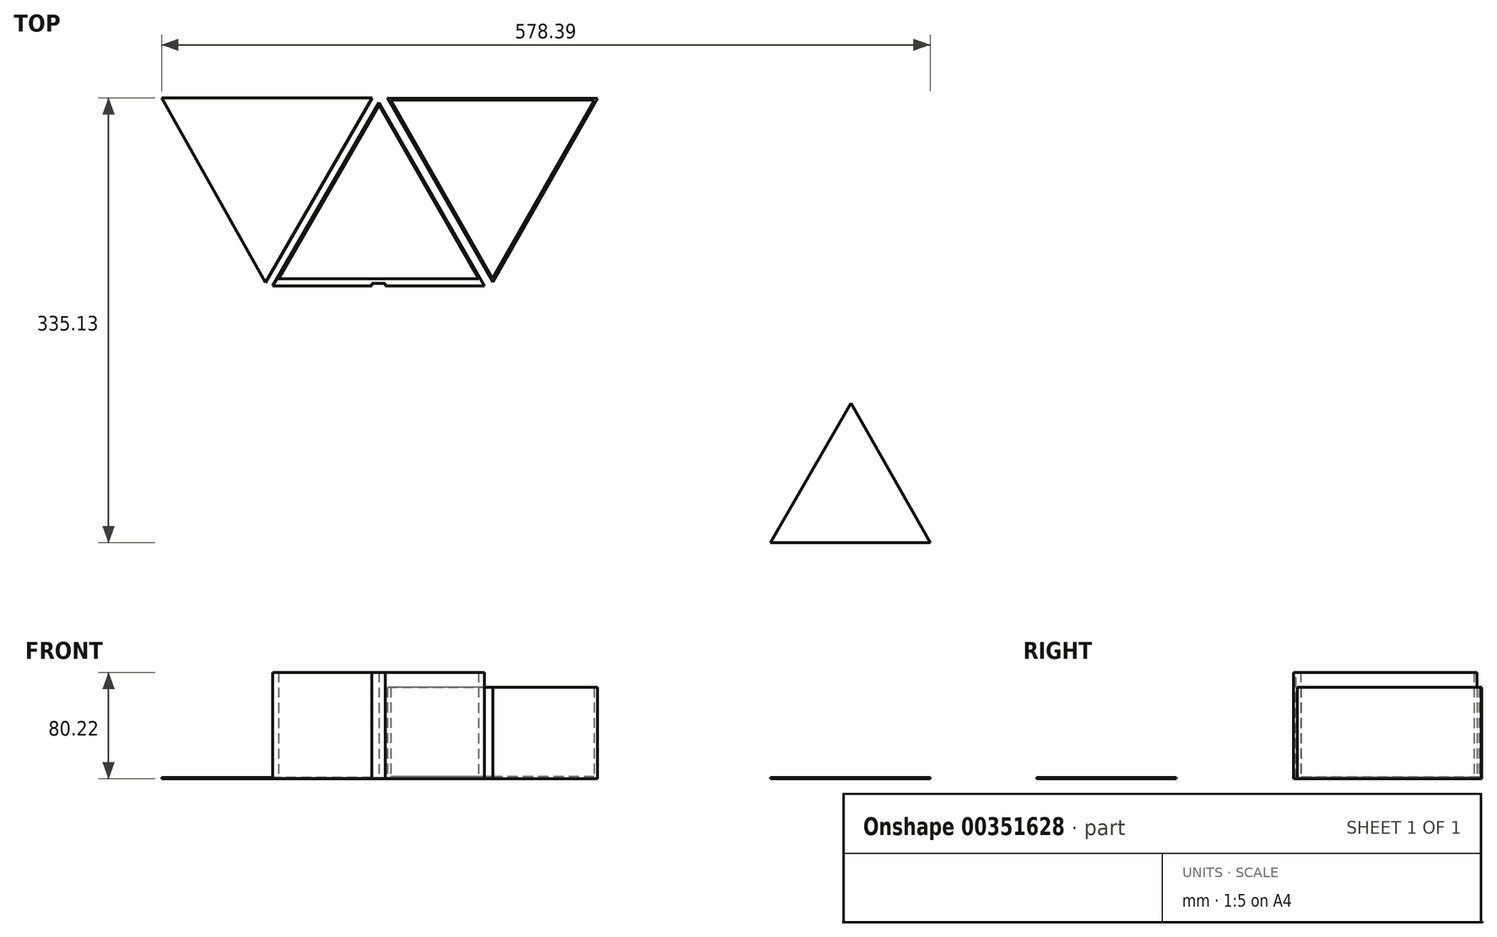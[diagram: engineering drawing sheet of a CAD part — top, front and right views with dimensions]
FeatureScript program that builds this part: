
annotation { "Feature Type Name" : "Feature", "Feature Type Description" : "" }
export const myFeature = defineFeature(function(context is Context, id is Id, definition is map)
    precondition{}
    {
        {
            var Q0;
            Q0=qCreatedBy(makeId("Top.planeOp"),FACE);
            var sketch = newSketch(context, id + "F0", { "sketchPlane" : qUnion([Q0])});
            skLineSegment(sketch, "E0", {"start": v(-204.44, 298.93) * mm, "end": v(-205.39, 298.47) * mm});
            skLineSegment(sketch, "E1", {"start": v(-46.32, 7.93) * mm, "end": v(-45.37, 8.4) * mm});
            skLineSegment(sketch, "E2", {"start": v(-289.5, 156.66) * mm, "end": v(-210.67, 295.29) * mm});
            skLineSegment(sketch, "E3", {"start": v(-289.2, 150.5) * mm, "end": v(-211.12, 11.46) * mm});
            skLineSegment(sketch, "E4", {"start": v(-205.5, 8.78) * mm, "end": v(-46.32, 8.78) * mm});
            skLineSegment(sketch, "E5", {"start": v(-40.08, 11.57) * mm, "end": v(38.74, 150.2) * mm});
            skLineSegment(sketch, "E6", {"start": v(-205.39, 298.47) * mm, "end": v(-45.26, 298.47) * mm});
            skLineSegment(sketch, "E7", {"start": v(-39.63, 295.4) * mm, "end": v(38.44, 156.38) * mm});
            skLineSegment(sketch, "E8", {"start": v(-289.5, 156.66) * mm, "end": v(38.44, 156.36) * mm});
            skLineSegment(sketch, "E9", {"start": v(38.74, 150.2) * mm, "end": v(-289.2, 150.5) * mm});
            skLineSegment(sketch, "E10", {"start": v(-211.12, 11.46) * mm, "end": v(-45.26, 298.09) * mm});
            skLineSegment(sketch, "E11", {"start": v(-39.63, 295.4) * mm, "end": v(-205.5, 8.78) * mm});
            skLineSegment(sketch, "E12", {"start": v(-46.32, 8.78) * mm, "end": v(-210.67, 295.29) * mm});
            skLineSegment(sketch, "E13", {"start": v(-204.44, 298.93) * mm, "end": v(-40.08, 11.57) * mm});
            skLineSegment(sketch, "E14", {"start": v(289.2, -184.63) * mm, "end": v(289.2, -190.5) * mm});
            skLineSegment(sketch, "E15", {"start": v(102.94, -76.2) * mm, "end": v(224.18, -76.2) * mm});
            skLineSegment(sketch, "E16", {"start": v(229.77, -79.25) * mm, "end": v(289.2, -184.63) * mm});
            skLineSegment(sketch, "E17", {"start": v(289.5, -190.8) * mm, "end": v(229.37, -295.76) * mm});
            skLineSegment(sketch, "E18", {"start": v(102.83, -298.53) * mm, "end": v(224.07, -298.53) * mm});
            skLineSegment(sketch, "E19", {"start": v(37.81, -190.5) * mm, "end": v(97.24, -295.87) * mm});
            skLineSegment(sketch, "E20", {"start": v(37.52, -184.33) * mm, "end": v(97.64, -79.37) * mm});
            skLineSegment(sketch, "E21", {"start": v(97.64, -79.37) * mm, "end": v(224.07, -298.93) * mm});
            skLineSegment(sketch, "E22", {"start": v(229.37, -295.77) * mm, "end": v(102.94, -76.2) * mm});
            skLineSegment(sketch, "E23", {"start": v(224.18, -76.6) * mm, "end": v(97.23, -295.87) * mm});
            skLineSegment(sketch, "E24", {"start": v(102.83, -298.53) * mm, "end": v(229.77, -79.25) * mm});
            skLineSegment(sketch, "E25", {"start": v(289.2, -184.63) * mm, "end": v(37.52, -184.33) * mm});
            skLineSegment(sketch, "E26", {"start": v(38.75, -190.5) * mm, "end": v(289.2, -190.5) * mm});
            skLineSegment(sketch, "E27", {"start": v(6.53, -0.37) * mm, "end": v(6.24, -0.67) * mm});
            skLineSegment(sketch, "E28", {"start": v(101.94, -34.7) * mm, "end": v(42.66, 67.95) * mm});
            skLineSegment(sketch, "E29", {"start": v(47.86, 71.28) * mm, "end": v(107.02, -31.78) * mm});
            skLineSegment(sketch, "E30", {"start": v(101.94, 39.85) * mm, "end": v(119.86, 70.9) * mm});
            skLineSegment(sketch, "E31", {"start": v(125.36, 68.08) * mm, "end": v(107.02, 36.91) * mm});
            skLineSegment(sketch, "E32", {"start": v(107.02, -31.78) * mm, "end": v(124.94, -62.83) * mm});
            skLineSegment(sketch, "E33", {"start": v(119.75, -66.16) * mm, "end": v(101.94, -34.7) * mm});
            skLineSegment(sketch, "E34", {"start": v(107.02, 36.91) * mm, "end": v(83.8, -3.3) * mm});
            skLineSegment(sketch, "E35", {"start": v(83.8, -3.3) * mm, "end": v(47.74, -65.77) * mm});
            skLineSegment(sketch, "E36", {"start": v(42.25, -62.96) * mm, "end": v(80.34, 2.68) * mm});
            skLineSegment(sketch, "E37", {"start": v(80.34, 2.68) * mm, "end": v(81.99, 5.5) * mm});
            skLineSegment(sketch, "E38", {"start": v(81.99, 5.5) * mm, "end": v(83.82, 8.64) * mm});
            skLineSegment(sketch, "E39", {"start": v(83.82, 8.64) * mm, "end": v(101.94, 39.85) * mm});
            skLineSegment(sketch, "E40", {"start": v(6.25, 5.79) * mm, "end": v(42.66, 67.95) * mm});
            skLineSegment(sketch, "E41", {"start": v(119.86, 70.9) * mm, "end": v(47.86, 71.28) * mm});
            skLineSegment(sketch, "E42", {"start": v(125.36, 68.08) * mm, "end": v(161.07, 5.5) * mm});
            skLineSegment(sketch, "E43", {"start": v(161.35, -0.67) * mm, "end": v(124.95, -62.82) * mm});
            skLineSegment(sketch, "E44", {"start": v(119.75, -66.16) * mm, "end": v(47.74, -65.77) * mm});
            skLineSegment(sketch, "E45", {"start": v(42.25, -62.96) * mm, "end": v(6.24, -0.67) * mm});
            skLineSegment(sketch, "E46", {"start": v(6.53, -0.37) * mm, "end": v(161.35, -0.37) * mm});
            skLineSegment(sketch, "E47", {"start": v(6.25, 5.79) * mm, "end": v(161.07, 5.79) * mm});
            skLineSegment(sketch, "E48", {"start": v(19.6, 227.08) * mm, "end": v(56.76, 226.79) * mm});
            skLineSegment(sketch, "E49", {"start": v(56.76, 226.79) * mm, "end": v(56.76, 225.15) * mm});
            skLineSegment(sketch, "E50", {"start": v(56.76, 225.15) * mm, "end": v(19.54, 225.5) * mm});
            skLineSegment(sketch, "E51", {"start": v(19.6, 227.08) * mm, "end": v(58.76, 293.92) * mm});
            skLineSegment(sketch, "E52", {"start": v(138.47, 293.92) * mm, "end": v(60.17, 294.38) * mm});
            skLineSegment(sketch, "E53", {"start": v(176.9, 224.62) * mm, "end": v(138, 157.9) * mm});
            skLineSegment(sketch, "E54", {"start": v(136.8, 157.2) * mm, "end": v(59, 157.64) * mm});
            skLineSegment(sketch, "E55", {"start": v(-188.29, -29.51) * mm, "end": v(-61.66, -29.51) * mm});
            skLineSegment(sketch, "E56", {"start": v(-60.45, -30.55) * mm, "end": v(1.91, -140.41) * mm});
            skLineSegment(sketch, "E57", {"start": v(1.9, -141.7) * mm, "end": v(-60.54, -251.53) * mm});
            skLineSegment(sketch, "E58", {"start": v(-189.74, -251.49) * mm, "end": v(-61.8, -251.85) * mm});
            skLineSegment(sketch, "E59", {"start": v(-253.87, -141.43) * mm, "end": v(-191.1, -251.3) * mm});
            skLineSegment(sketch, "E60", {"start": v(-253.64, -140.12) * mm, "end": v(-189.46, -29.84) * mm});
            skLineSegment(sketch, "E61", {"start": v(-253.64, -140.12) * mm, "end": v(-192.03, -140.44) * mm});
            skLineSegment(sketch, "E62", {"start": v(-192.03, -140.44) * mm, "end": v(-191.86, -141.7) * mm});
            skLineSegment(sketch, "E63", {"start": v(-191.86, -141.7) * mm, "end": v(-253.87, -141.43) * mm});
            skLineSegment(sketch, "E64", {"start": v(-59.46, -140.07) * mm, "end": v(1.9, -140.3) * mm});
            skLineSegment(sketch, "E65", {"start": v(1.9, -140.3) * mm, "end": v(1.9, -141.7) * mm});
            skLineSegment(sketch, "E66", {"start": v(1.9, -141.7) * mm, "end": v(-59.46, -141.47) * mm});
            skLineSegment(sketch, "E67", {"start": v(-59.46, -140.07) * mm, "end": v(-59.46, -141.47) * mm});
            skLineSegment(sketch, "E68", {"start": v(-92.6, -82.83) * mm, "end": v(-61.66, -29.84) * mm});
            skLineSegment(sketch, "E69", {"start": v(-61.66, -29.84) * mm, "end": v(-60.45, -30.55) * mm});
            skLineSegment(sketch, "E70", {"start": v(-60.45, -30.55) * mm, "end": v(-91.64, -84) * mm});
            skLineSegment(sketch, "E71", {"start": v(-191.1, -251.3) * mm, "end": v(-159.76, -197.34) * mm});
            skLineSegment(sketch, "E72", {"start": v(-159.76, -197.34) * mm, "end": v(-158.55, -198.04) * mm});
            skLineSegment(sketch, "E73", {"start": v(-158.55, -198.04) * mm, "end": v(-189.74, -251.49) * mm});
            skLineSegment(sketch, "E74", {"start": v(-60.58, -251.49) * mm, "end": v(-93.25, -198.04) * mm});
            skLineSegment(sketch, "E75", {"start": v(-93.25, -198.04) * mm, "end": v(-94.06, -199.31) * mm});
            skLineSegment(sketch, "E76", {"start": v(-94.06, -199.31) * mm, "end": v(-61.69, -252.04) * mm});
            skLineSegment(sketch, "E77", {"start": v(-157.6, -83.17) * mm, "end": v(-188.63, -28.75) * mm});
            skLineSegment(sketch, "E78", {"start": v(-188.63, -28.75) * mm, "end": v(-189.48, -30) * mm});
            skLineSegment(sketch, "E79", {"start": v(-189.48, -30) * mm, "end": v(-158.72, -83.7) * mm});
            skLineSegment(sketch, "E80", {"start": v(-158.72, -83.7) * mm, "end": v(-157.6, -83.17) * mm});
            skLineSegment(sketch, "E81", {"start": v(-92.6, -82.83) * mm, "end": v(-91.64, -84) * mm});
            skLineSegment(sketch, "E82", {"start": v(60.17, 294.38) * mm, "end": v(78.36, 262.01) * mm});
            skLineSegment(sketch, "E83", {"start": v(78.36, 262.01) * mm, "end": v(77.14, 261.32) * mm});
            skLineSegment(sketch, "E84", {"start": v(77.14, 261.32) * mm, "end": v(58.76, 293.92) * mm});
            skLineSegment(sketch, "E85", {"start": v(139.88, 293.22) * mm, "end": v(119.58, 260.06) * mm});
            skLineSegment(sketch, "E86", {"start": v(119.58, 260.06) * mm, "end": v(118.38, 260.77) * mm});
            skLineSegment(sketch, "E87", {"start": v(118.38, 260.77) * mm, "end": v(138.47, 293.92) * mm});
            skLineSegment(sketch, "E88", {"start": v(78.22, 189.85) * mm, "end": v(59, 157.64) * mm});
            skLineSegment(sketch, "E89", {"start": v(57.93, 158.6) * mm, "end": v(76.91, 190.34) * mm});
            skLineSegment(sketch, "E90", {"start": v(119.47, 190.78) * mm, "end": v(138, 157.9) * mm});
            skLineSegment(sketch, "E91", {"start": v(136.8, 157.2) * mm, "end": v(118.25, 190.09) * mm});
            skLineSegment(sketch, "E92", {"start": v(176.9, 224.62) * mm, "end": v(139.73, 224.92) * mm});
            skLineSegment(sketch, "E93", {"start": v(139.73, 224.92) * mm, "end": v(139.73, 226.56) * mm});
            skLineSegment(sketch, "E94", {"start": v(139.73, 226.56) * mm, "end": v(176.95, 226.2) * mm});
            skLineSegment(sketch, "E95", {"start": v(78.22, 189.85) * mm, "end": v(76.91, 190.34) * mm});
            skLineSegment(sketch, "E96", {"start": v(118.25, 190.09) * mm, "end": v(119.47, 190.78) * mm});
            skLineSegment(sketch, "E97", {"start": v(119.91, 114.23) * mm, "end": v(157.08, 113.93) * mm});
            skLineSegment(sketch, "E98", {"start": v(157.08, 113.93) * mm, "end": v(157.08, 112.3) * mm});
            skLineSegment(sketch, "E99", {"start": v(157.08, 112.3) * mm, "end": v(119.86, 112.65) * mm});
            skLineSegment(sketch, "E100", {"start": v(119.91, 114.23) * mm, "end": v(159.08, 181.07) * mm});
            skLineSegment(sketch, "E101", {"start": v(238.75, 181.07) * mm, "end": v(160.65, 181.49) * mm});
            skLineSegment(sketch, "E102", {"start": v(239.46, 179.93) * mm, "end": v(277.27, 113.35) * mm});
            skLineSegment(sketch, "E103", {"start": v(277.22, 111.77) * mm, "end": v(238.18, 45.32) * mm});
            skLineSegment(sketch, "E104", {"start": v(236.96, 44.4) * mm, "end": v(158.88, 44.79) * mm});
            skLineSegment(sketch, "E105", {"start": v(158.88, 44.65) * mm, "end": v(119.97, 112.54) * mm});
            skLineSegment(sketch, "E106", {"start": v(160.65, 181.49) * mm, "end": v(178.68, 149.16) * mm});
            skLineSegment(sketch, "E107", {"start": v(178.68, 149.16) * mm, "end": v(177.46, 148.47) * mm});
            skLineSegment(sketch, "E108", {"start": v(177.46, 148.47) * mm, "end": v(159.08, 181.07) * mm});
            skLineSegment(sketch, "E109", {"start": v(239.46, 179.93) * mm, "end": v(219.9, 147.2) * mm});
            skLineSegment(sketch, "E110", {"start": v(219.9, 147.2) * mm, "end": v(218.7, 147.92) * mm});
            skLineSegment(sketch, "E111", {"start": v(218.7, 147.92) * mm, "end": v(238.75, 181.07) * mm});
            skLineSegment(sketch, "E112", {"start": v(178.8, 77.38) * mm, "end": v(159.23, 44.65) * mm});
            skLineSegment(sketch, "E113", {"start": v(159.23, 44.65) * mm, "end": v(158.03, 45.36) * mm});
            skLineSegment(sketch, "E114", {"start": v(158.03, 45.36) * mm, "end": v(177.23, 77.49) * mm});
            skLineSegment(sketch, "E115", {"start": v(219.79, 77.92) * mm, "end": v(238.18, 45.32) * mm});
            skLineSegment(sketch, "E116", {"start": v(238.18, 45.32) * mm, "end": v(236.96, 44.63) * mm});
            skLineSegment(sketch, "E117", {"start": v(236.96, 44.63) * mm, "end": v(218.57, 77.23) * mm});
            skLineSegment(sketch, "E118", {"start": v(277.22, 111.77) * mm, "end": v(240.05, 112.07) * mm});
            skLineSegment(sketch, "E119", {"start": v(240.05, 112.07) * mm, "end": v(240.05, 113.7) * mm});
            skLineSegment(sketch, "E120", {"start": v(240.05, 113.7) * mm, "end": v(277.27, 113.35) * mm});
            skLineSegment(sketch, "E121", {"start": v(178.8, 77.38) * mm, "end": v(177.23, 77.49) * mm});
            skLineSegment(sketch, "E122", {"start": v(218.57, 77.23) * mm, "end": v(219.79, 77.93) * mm});
            skLineSegment(sketch, "E123.trimOffspring", {"start": v(57.93, 158.6) * mm, "end": v(19.54, 225.5) * mm});
            skLineSegment(sketch, "E124", {"start": v(139.88, 293.22) * mm, "end": v(176.95, 226.2) * mm});
            skLineSegment(sketch, "E125", {"start": v(60.17, 294.38) * mm, "end": v(138.47, 293.92) * mm});
            skLineSegment(sketch, "E126", {"start": v(138.47, 293.92) * mm, "end": v(118.38, 260.77) * mm});
            skLineSegment(sketch, "E127", {"start": v(118.38, 260.77) * mm, "end": v(119.58, 260.06) * mm});
            skLineSegment(sketch, "E128", {"start": v(119.58, 260.06) * mm, "end": v(139.88, 293.22) * mm});
            skLineSegment(sketch, "E129", {"start": v(176.95, 226.2) * mm, "end": v(139.73, 226.56) * mm});
            skLineSegment(sketch, "E130", {"start": v(139.73, 226.56) * mm, "end": v(139.73, 224.92) * mm});
            skLineSegment(sketch, "E131", {"start": v(139.73, 224.92) * mm, "end": v(176.9, 224.62) * mm});
            skLineSegment(sketch, "E132", {"start": v(138, 157.9) * mm, "end": v(119.47, 190.78) * mm});
            skLineSegment(sketch, "E133", {"start": v(118.25, 190.09) * mm, "end": v(136.8, 157.2) * mm});
            skLineSegment(sketch, "E134", {"start": v(59, 157.64) * mm, "end": v(78.22, 189.85) * mm});
            skLineSegment(sketch, "E135", {"start": v(76.91, 190.34) * mm, "end": v(57.93, 158.6) * mm});
            skLineSegment(sketch, "E136", {"start": v(19.54, 225.5) * mm, "end": v(56.76, 225.15) * mm});
            skLineSegment(sketch, "E137", {"start": v(56.76, 226.79) * mm, "end": v(19.6, 227.08) * mm});
            skLineSegment(sketch, "E138", {"start": v(58.76, 293.92) * mm, "end": v(77.14, 261.32) * mm});
            skLineSegment(sketch, "E139.0", {"start": v(-38.76, 294.9) * mm, "end": v(-204.64, 8.28) * mm, "construction": true});
            skSolve(sketch);
        }
        {
            var Q0;
            {var subQ0=sQuery(id+"F0.wireOp",EDGE,"E4");Q0=makeQuery(id+"F0.imprint","IMPRINT",FACE,{"disambiguationData":[TD([[makeQuery(id+"F0.imprint","IMPRINT",EDGE,{"derivedFrom":subQ0}),1.0]])]});}
            extrude(context, id + "F1", {"entities" : qUnion([Q0]), "depth" : 1 * mm});
        }
        {
            var Q0;
            {var subQ0=sQuery(id+"F0.wireOp",EDGE,"E16");Q0=makeQuery(id+"F0.imprint","IMPRINT",FACE,{"disambiguationData":[TD([[makeQuery(id+"F0.imprint","IMPRINT",EDGE,{"derivedFrom":subQ0}),-1.0]])]});}
            extrude(context, id + "F2", {"entities" : qUnion([Q0]), "depth" : 1 * mm});
        }
        {
            var Q0;
            Q0=makeQuery(id+"F1.opExtrude","CAP_FACE",FACE,{"disambiguationData":[OSD([sQuery(id+"F0.wireOp",EDGE,"E4"),sQuery(id+"F0.wireOp",EDGE,"E11"),sQuery(id+"F0.wireOp",EDGE,"E12")])],"isStart":false});
            var sketch = newSketch(context, id + "F3", { "sketchPlane" : qUnion([Q0])});
            skLineSegment(sketch, "E140.0", {"start": v(-203.8, 9.78) * mm, "end": v(-46.32, 9.78) * mm, "construction": true});
            skLineSegment(sketch, "E141.0", {"start": v(-47.2, 8.28) * mm, "end": v(-211.54, 294.8) * mm, "construction": true});
            skLineSegment(sketch, "E142", {"start": v(-203.8, 9.78) * mm, "end": v(-125.57, 144.91) * mm});
            skLineSegment(sketch, "E143", {"start": v(-125.57, 144.91) * mm, "end": v(-48.05, 9.78) * mm});
            skLineSegment(sketch, "E144", {"start": v(-203.8, 9.78) * mm, "end": v(-48.05, 9.78) * mm});
            skLineSegment(sketch, "E145", {"start": v(-204.92, 9.78) * mm, "end": v(-203.8, 9.78) * mm});
            skLineSegment(sketch, "E146", {"start": v(-201.18, 14.32) * mm, "end": v(-50.65, 14.32) * mm});
            skLineSegment(sketch, "E147", {"start": v(-125.91, 8.78) * mm, "end": v(-125.91, 14.32) * mm, "construction": true});
            skLineSegment(sketch, "E148.0", {"start": v(-120.91, 8.78) * mm, "end": v(-120.91, 14.32) * mm, "construction": true});
            skLineSegment(sketch, "E149.0", {"start": v(-130.91, 8.78) * mm, "end": v(-130.91, 14.32) * mm, "construction": true});
            skLineSegment(sketch, "E150", {"start": v(-130.91, 14.32) * mm, "end": v(-130.91, 8.78) * mm, "construction": true});
            skSolve(sketch);
        }
        {
            var Q0;
            Q0=makeQuery(id+"F3.imprint","IMPRINT",FACE,{"disambiguationData":[TD([[makeQuery(id+"F3.imprint","IMPRINT",EDGE,{"derivedFrom":sQuery(id+"F3.wireOp",EDGE,"E142")}),1.0]])]});
            extrude(context, id + "F4", {"entities" : qUnion([Q0]), "operationType" : NewBodyOperationType.ADD, "depth" : 79.22 * mm});
        }
        {
            var Q0;
            {var subQ0=sQuery(id+"F3.wireOp",EDGE,"E144");Q0=makeQuery(id+"F3.imprint","IMPRINT",FACE,{"disambiguationData":[TD([[makeQuery(id+"F3.imprint","IMPRINT",EDGE,{"derivedFrom":subQ0}),1.0]])]});}
            extrude(context, id + "F5", {"entities" : qUnion([Q0]), "operationType" : NewBodyOperationType.ADD, "depth" : 79.22 * mm});
        }
        {
            var Q0;
            {var subQ0=sQuery(id+"F0.wireOp",EDGE,"E4");Q0=makeQuery(id+"F4.boolean.opBoolean","MERGE",FACE,{"derivedFrom":[makeQuery(id+"F1.opExtrude","SWEPT_FACE",FACE,{"disambiguationData":[OSD([subQ0])]}),makeQuery(id+"F4.opExtrude","SWEPT_FACE",FACE,{"disambiguationData":[OSD([subQ0])]})]});}
            var sketch = newSketch(context, id + "F6", { "sketchPlane" : qUnion([Q0])});
            skLineSegment(sketch, "E151.0", {"start": v(-210.5, -5) * mm, "end": v(-41.32, -5) * mm, "construction": true});
            skLineSegment(sketch, "E151.1", {"start": v(-210.5, 85.22) * mm, "end": v(-210.5, -5) * mm, "construction": true});
            skLineSegment(sketch, "E151.2", {"start": v(-41.32, 85.22) * mm, "end": v(-210.5, 85.22) * mm, "construction": true});
            skLineSegment(sketch, "E151.3", {"start": v(-41.32, -5) * mm, "end": v(-41.32, 85.22) * mm, "construction": true});
            skLineSegment(sketch, "E152.0", {"start": v(-120.91, 0) * mm, "end": v(-120.91, 80.22) * mm, "construction": true});
            skLineSegment(sketch, "E153.0", {"start": v(-130.91, 0) * mm, "end": v(-130.91, 80.22) * mm, "construction": true});
            skLineSegment(sketch, "E154", {"start": v(-120.91, 80.22) * mm, "end": v(-120.91, 0) * mm, "construction": true});
            skPoint(sketch, "E155.end.orphan", {"position": v(-125.91, 80.22) * mm});
            skPoint(sketch, "E155.start.orphan", {"position": v(-125.91, 0) * mm});
            skLineSegment(sketch, "E156", {"start": v(-130.91, 0) * mm, "end": v(-130.91, 80.22) * mm});
            skLineSegment(sketch, "E157", {"start": v(-120.91, 0) * mm, "end": v(-120.91, 80.22) * mm});
            skLineSegment(sketch, "E158", {"start": v(-130.91, 0) * mm, "end": v(-120.91, 0) * mm});
            skLineSegment(sketch, "E159", {"start": v(-120.91, 80.22) * mm, "end": v(-130.91, 80.22) * mm});
            skSolve(sketch);
        }
        {
            var Q0;
            {var subQ0=sQuery(id+"F3.wireOp",EDGE,"E144");var subQ1=sQuery(id+"F3.wireOp",EDGE,"E143");var subQ2=sQuery(id+"F3.wireOp",EDGE,"E142");Q0=makeQuery(id+"F5.boolean.opBoolean","MERGE",FACE,{"derivedFrom":[makeQuery(id+"F4.opExtrude","CAP_FACE",FACE,{"disambiguationData":[OSD([sQuery(id+"F0.wireOp",EDGE,"E4"),sQuery(id+"F0.wireOp",EDGE,"E11"),sQuery(id+"F0.wireOp",EDGE,"E12"),subQ2,subQ1,subQ0])],"isStart":false}),makeQuery(id+"F5.opExtrude","CAP_FACE",FACE,{"disambiguationData":[OSD([subQ2,subQ1,subQ0,sQuery(id+"F3.wireOp",EDGE,"E146")])],"isStart":false})]});}
            var sketch = newSketch(context, id + "F7", { "sketchPlane" : qUnion([Q0])});
            skLineSegment(sketch, "E160", {"start": v(-131.11, 8.78) * mm, "end": v(-131.11, 14.32) * mm});
            skLineSegment(sketch, "E161", {"start": v(-121.02, 8.78) * mm, "end": v(-121.02, 14.32) * mm});
            skSolve(sketch);
        }
        {
            var Q0;
            Q0=makeQuery(id+"F6.imprint","IMPRINT",FACE,{"disambiguationData":[TD([[makeQuery(id+"F6.imprint","IMPRINT",EDGE,{"derivedFrom":sQuery(id+"F6.wireOp",EDGE,"E156")}),-1.0]])]});
            extrude(context, id + "F8", {"entities" : qUnion([Q0]), "operationType" : NewBodyOperationType.REMOVE, "oppositeDirection" : true, "depth" : 2 * mm});
        }
        {
            var Q0;
            {var subQ0=sQuery(id+"F0.wireOp",EDGE,"E3");Q0=makeQuery(id+"F0.imprint","IMPRINT",FACE,{"disambiguationData":[TD([[makeQuery(id+"F0.imprint","IMPRINT",EDGE,{"derivedFrom":subQ0}),1.0]])]});}
            extrude(context, id + "F9", {"entities" : qUnion([Q0]), "depth" : 1 * mm});
        }
        {
            var Q0;
            {var subQ0=sQuery(id+"F0.wireOp",EDGE,"E5");Q0=makeQuery(id+"F0.imprint","IMPRINT",FACE,{"disambiguationData":[TD([[makeQuery(id+"F0.imprint","IMPRINT",EDGE,{"derivedFrom":subQ0}),1.0]])]});}
            extrude(context, id + "F10", {"entities" : qUnion([Q0]), "depth" : 1.5 * mm});
        }
        {
            var Q0;
            Q0=makeQuery(id+"F10.opExtrude","CAP_FACE",FACE,{"disambiguationData":[OSD([sQuery(id+"F0.wireOp",EDGE,"E5"),sQuery(id+"F0.wireOp",EDGE,"E9"),sQuery(id+"F0.wireOp",EDGE,"E13")])],"isStart":false});
            var sketch = newSketch(context, id + "F11", { "sketchPlane" : qUnion([Q0])});
            skLineSegment(sketch, "E162", {"start": v(-116.87, 148.84) * mm, "end": v(36.16, 148.7) * mm, "construction": true});
            skLineSegment(sketch, "E163", {"start": v(36.16, 148.7) * mm, "end": v(-116.87, 148.84) * mm});
            skLineSegment(sketch, "E164", {"start": v(-116.87, 148.84) * mm, "end": v(-40.08, 14.6) * mm, "construction": true});
            skLineSegment(sketch, "E165", {"start": v(-40.08, 14.6) * mm, "end": v(-116.87, 148.84) * mm});
            skLineSegment(sketch, "E166", {"start": v(-40.08, 14.6) * mm, "end": v(36.16, 148.7) * mm});
            skSolve(sketch);
        }
        {
            var Q0;
            Q0=makeQuery(id+"F11.imprint","IMPRINT",FACE,{"disambiguationData":[TD([[makeQuery(id+"F11.imprint","IMPRINT",EDGE,{"derivedFrom":sQuery(id+"F11.wireOp",EDGE,"E163")}),-1.0]])]});
            extrude(context, id + "F12", {"entities" : qUnion([Q0]), "operationType" : NewBodyOperationType.ADD, "depth" : 67.4 * mm});
        }
    });
